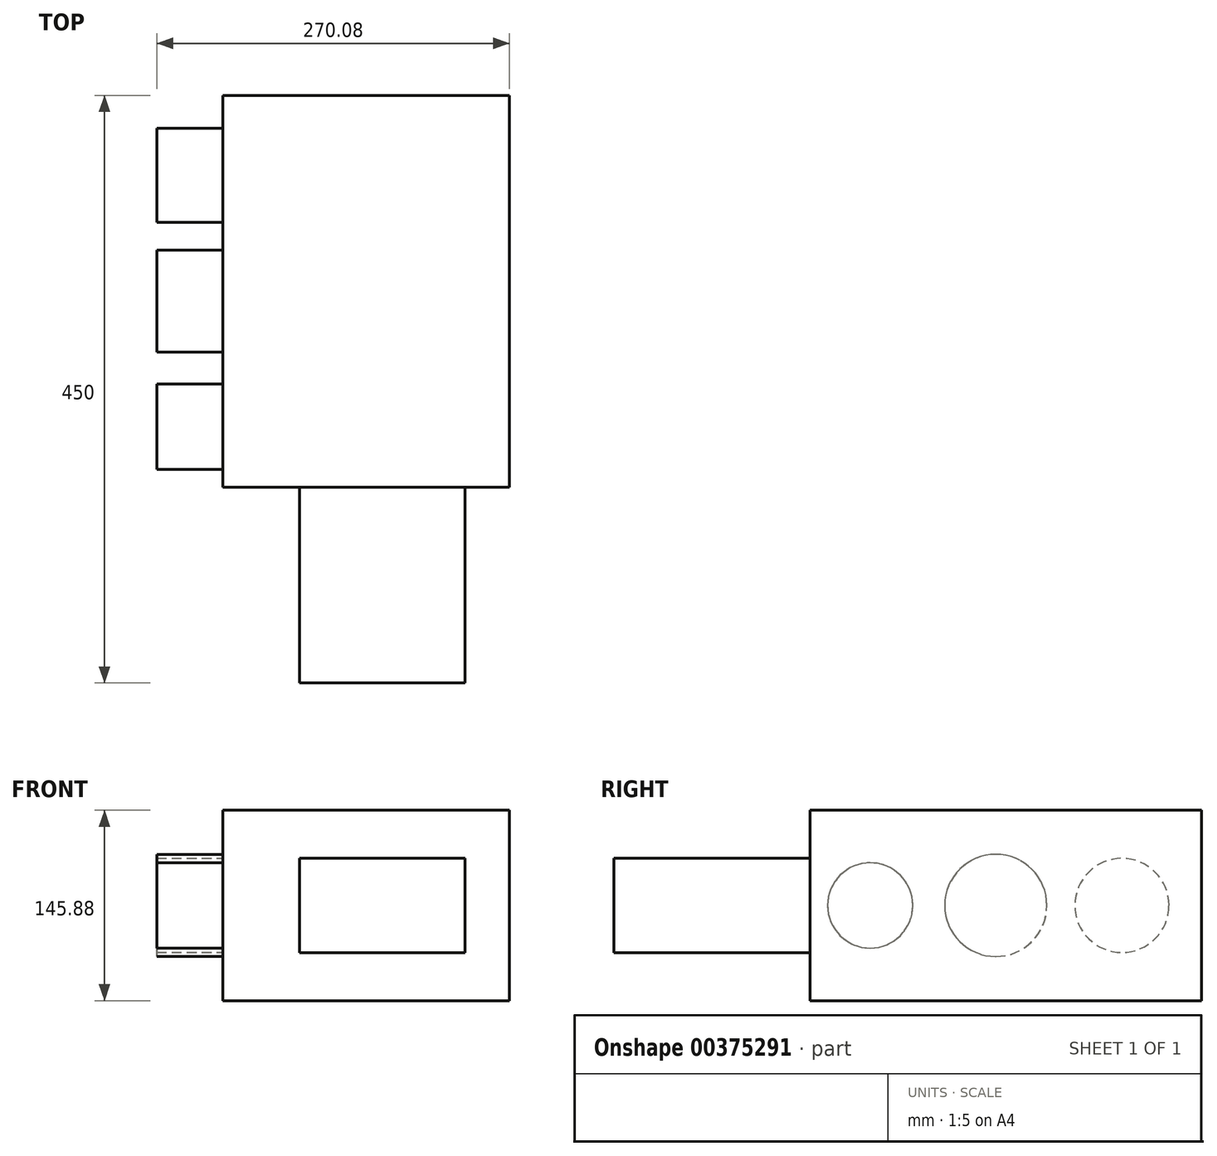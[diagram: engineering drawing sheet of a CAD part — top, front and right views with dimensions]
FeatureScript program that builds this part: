
annotation { "Feature Type Name" : "Feature", "Feature Type Description" : "" }
export const myFeature = defineFeature(function(context is Context, id is Id, definition is map)
    precondition{}
    {
        {
            var Q0;
            Q0=qCreatedBy(makeId("Front.planeOp"),FACE);
            var sketch = newSketch(context, id + "F0", { "sketchPlane" : qUnion([Q0])});
            skLineSegment(sketch, "E0.bottom", {"start": v(75.93, 36.1) * mm, "end": v(-75.93, 36.1) * mm});
            skLineSegment(sketch, "E0.top", {"start": v(75.93, -36.1) * mm, "end": v(-75.93, -36.1) * mm});
            skLineSegment(sketch, "E0.left", {"start": v(75.93, 36.1) * mm, "end": v(75.93, -36.1) * mm});
            skLineSegment(sketch, "E0.right", {"start": v(-75.93, 36.1) * mm, "end": v(-75.93, -36.1) * mm});
            skPoint(sketch, "E0.middle", {"position": v(0, 0) * mm});
            skSolve(sketch);
        }
        {
            var Q0;
            Q0 = qSketchRegion(id + "F0", true);
            extrude(context, id + "F1", {"entities" : qUnion([Q0]), "depth" : 150 * mm});
        }
        {
            var Q0;
            Q0=makeQuery(id+"F1.opExtrude","CAP_FACE",FACE,{"disambiguationData":[OSD([sQuery(id+"F0.wireOp",EDGE,"E0.bottom"),sQuery(id+"F0.wireOp",EDGE,"E0.top"),sQuery(id+"F0.wireOp",EDGE,"E0.left"),sQuery(id+"F0.wireOp",EDGE,"E0.right")])],"isStart":true});
            var sketch = newSketch(context, id + "F2", { "sketchPlane" : qUnion([Q0])});
            skLineSegment(sketch, "E1.bottom", {"start": v(-134.64, -72.94) * mm, "end": v(134.64, -72.94) * mm});
            skLineSegment(sketch, "E1.top", {"start": v(-134.64, 72.94) * mm, "end": v(134.64, 72.94) * mm});
            skLineSegment(sketch, "E1.left", {"start": v(-134.64, -72.94) * mm, "end": v(-134.64, 72.94) * mm});
            skLineSegment(sketch, "E1.right", {"start": v(134.64, -72.94) * mm, "end": v(134.64, 72.94) * mm});
            skPoint(sketch, "E1.middle", {"position": v(0, 0) * mm});
            skSolve(sketch);
        }
        {
            var Q0;
            Q0 = qSketchRegion(id + "F2", true);
            extrude(context, id + "F3", {"entities" : qUnion([Q0]), "operationType" : NewBodyOperationType.ADD, "depth" : 300 * mm});
        }
        {
            var Q0;
            Q0=makeQuery(id+"F3.opExtrude","SWEPT_FACE",FACE,{"disambiguationData":[OSD([sQuery(id+"F2.wireOp",EDGE,"E1.right")])]});
            var sketch = newSketch(context, id + "F4", { "sketchPlane" : qUnion([Q0])});
            skCircle(sketch, "E2", {"center": v(-238.9, 0) * mm, "radius": 36.05 * mm});
            skPoint(sketch, "E2.centerSnap0", {"position": v(-300, 0) * mm});
            skCircle(sketch, "E3", {"center": v(-142.35, 0) * mm, "radius": 39.11 * mm});
            skCircle(sketch, "E4", {"center": v(-46.22, 0) * mm, "radius": 32.63 * mm});
            skSolve(sketch);
        }
        {
            var Q0;
            Q0=makeQuery(id+"F3.opExtrude","SWEPT_FACE",FACE,{"disambiguationData":[OSD([sQuery(id+"F2.wireOp",EDGE,"E1.top")])]});
            var sketch = newSketch(context, id + "F5", { "sketchPlane" : qUnion([Q0])});
            skSolve(sketch);
        }
        {
            var Q0;
            Q0=makeQuery(id+"F4.imprint","IMPRINT",FACE,{"disambiguationData":[TD([[makeQuery(id+"F4.imprint","IMPRINT",EDGE,{"derivedFrom":sQuery(id+"F4.wireOp",EDGE,"E3")}),1.0]])]});
            var Q1;
            Q1 = qSketchRegion(id + "F4", true);
            extrude(context, id + "F6", {"entities" : qUnion([Q0, Q1]), "operationType" : NewBodyOperationType.ADD, "depth" : 25.4 * mm});
        }
        {
            var Q0;
            Q0=makeQuery(id+"F3.opExtrude","SWEPT_FACE",FACE,{"disambiguationData":[OSD([sQuery(id+"F2.wireOp",EDGE,"E1.left")])]});
            extrude(context, id + "F7", {"entities" : qUnion([Q0]), "operationType" : NewBodyOperationType.REMOVE, "oppositeDirection" : true, "depth" : 50 * mm});
        }
        {
            var Q0;
            Q0=makeQuery(id+"F1.opExtrude","SWEPT_FACE",FACE,{"disambiguationData":[OSD([sQuery(id+"F0.wireOp",EDGE,"E0.left")])]});
            extrude(context, id + "F8", {"entities" : qUnion([Q0]), "operationType" : NewBodyOperationType.REMOVE, "oppositeDirection" : true, "depth" : 25.4 * mm});
        }
        {
            var Q0;
            Q0=makeQuery(id+"F6.opExtrude","CAP_FACE",FACE,{"disambiguationData":[OSD([sQuery(id+"F4.wireOp",EDGE,"E2")])],"isStart":false});
            var Q1;
            Q1=makeQuery(id+"F6.opExtrude","CAP_FACE",FACE,{"disambiguationData":[OSD([sQuery(id+"F4.wireOp",EDGE,"E3")])],"isStart":false});
            var Q2;
            Q2=makeQuery(id+"F6.opExtrude","CAP_FACE",FACE,{"disambiguationData":[OSD([sQuery(id+"F4.wireOp",EDGE,"E4")])],"isStart":false});
            extrude(context, id + "F9", {"entities" : qUnion([Q0, Q1, Q2]), "operationType" : NewBodyOperationType.ADD, "depth" : 25.4 * mm});
        }
        {
            var Q0;
            {var subQ0=sQuery(id+"F2.wireOp",EDGE,"E1.top");Q0=makeQuery(id+"F5.imprint","IMPRINT",FACE,{"disambiguationData":[TD([[makeQuery(id+"F5.imprint","IMPRINT",EDGE,{"derivedFrom":makeQuery(id+"F3.opExtrude","CAP_EDGE",EDGE,{"disambiguationData":[OSD([subQ0])],"isStart":true})}),-1.0]])]});}
            extrude(context, id + "F10", {"entities" : qUnion([Q0]), "operationType" : NewBodyOperationType.REMOVE, "oppositeDirection" : true, "depth" : 25.4 * mm});
        }
        {
            var Q0;
            Q0=makeQuery(id+"F10.boolean.opBoolean","COPY",FACE,{"derivedFrom":makeQuery(id+"F10.opExtrude","CAP_FACE",FACE,{"disambiguationData":[OSD([sQuery(id+"F2.wireOp",EDGE,"E1.top"),sQuery(id+"F2.wireOp",EDGE,"E1.left"),sQuery(id+"F2.wireOp",EDGE,"E1.right")])],"isStart":false})});
            extrude(context, id + "F11", {"entities" : qUnion([Q0]), "operationType" : NewBodyOperationType.ADD, "depth" : 25.4 * mm});
        }
    });
